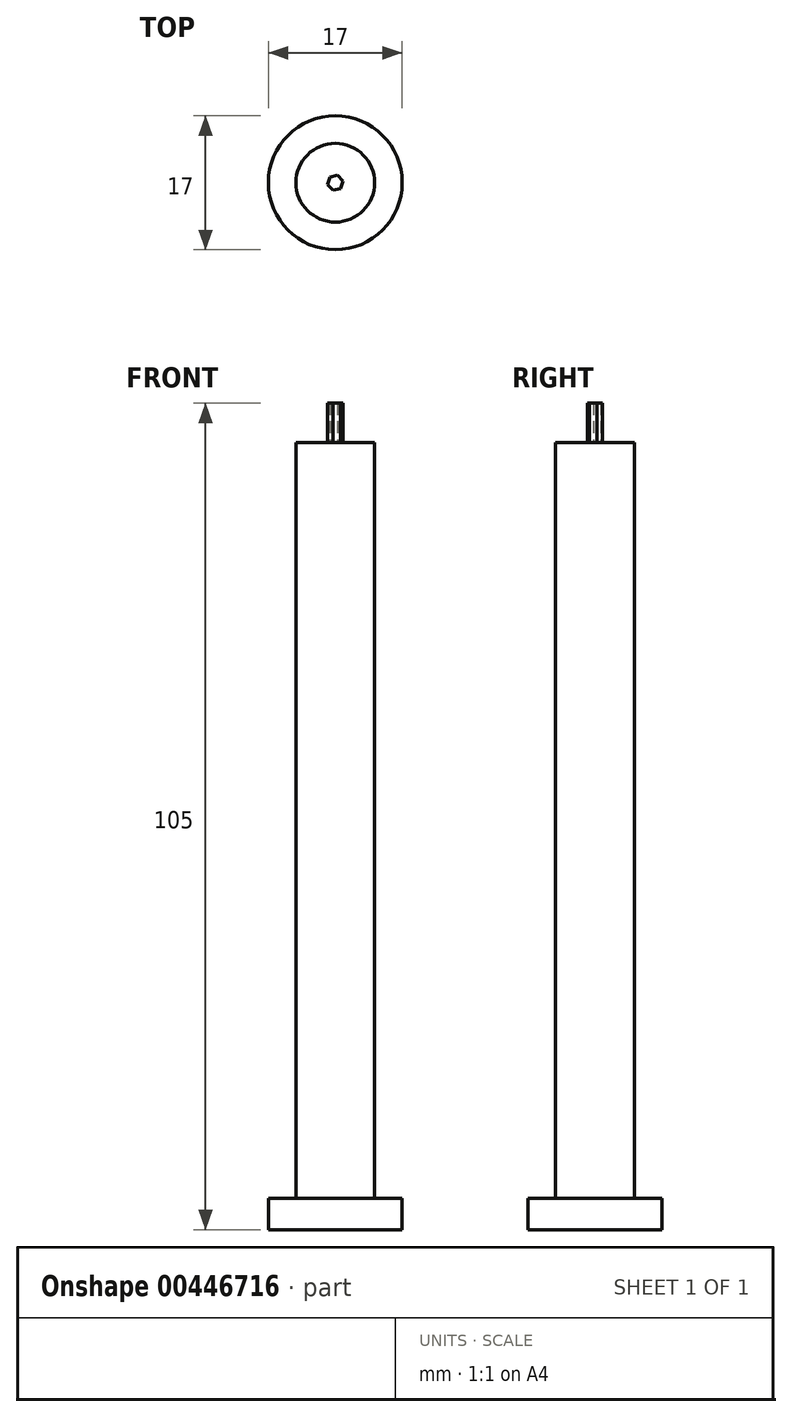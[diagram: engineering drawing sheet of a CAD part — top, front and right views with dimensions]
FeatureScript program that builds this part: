
annotation { "Feature Type Name" : "Feature", "Feature Type Description" : "" }
export const myFeature = defineFeature(function(context is Context, id is Id, definition is map)
    precondition{}
    {
        {
            var Q0;
            Q0=qCreatedBy(makeId("Top.planeOp"),FACE);
            var sketch = newSketch(context, id + "F0", { "sketchPlane" : qUnion([Q0])});
            skCircle(sketch, "E0", {"center": v(0, 0) * mm, "radius": 8.5 * mm});
            skSolve(sketch);
        }
        {
            var Q0;
            Q0=qSketchRegion(id+"F0",true);
            extrude(context, id + "F1", {"entities" : qUnion([Q0]), "depth" : 4 * mm});
        }
        {
            var Q0;
            Q0=qCreatedBy(makeId("Top.planeOp"),FACE);
            var sketch = newSketch(context, id + "F2", { "sketchPlane" : qUnion([Q0])});
            skCircle(sketch, "E1", {"center": v(0, 0) * mm, "radius": 5 * mm});
            skSolve(sketch);
        }
        {
            var Q0;
            Q0=qSketchRegion(id+"F2",true);
            extrude(context, id + "F3", {"entities" : qUnion([Q0]), "operationType" : NewBodyOperationType.ADD, "depth" : 100 * mm});
        }
        {
            var Q0;
            Q0=makeQuery(id+"F3.opExtrude","CAP_FACE",FACE,{"disambiguationData":[OSD([sQuery(id+"F2.wireOp",EDGE,"E1")])],"isStart":false});
            var sketch = newSketch(context, id + "F4", { "sketchPlane" : qUnion([Q0])});
            skCircle(sketch, "E2.cCircle", {"center": v(0, 0) * mm, "radius": 0.87 * mm, "construction": true});
            skLineSegment(sketch, "E2.0", {"start": v(0.98, 0.22) * mm, "end": v(0.67, -0.74) * mm});
            skLineSegment(sketch, "E2.1", {"start": v(0.67, -0.74) * mm, "end": v(-0.3, -0.95) * mm});
            skLineSegment(sketch, "E2.2", {"start": v(-0.3, -0.95) * mm, "end": v(-0.98, -0.22) * mm});
            skLineSegment(sketch, "E2.3", {"start": v(-0.98, -0.22) * mm, "end": v(-0.67, 0.74) * mm});
            skLineSegment(sketch, "E2.4", {"start": v(-0.67, 0.74) * mm, "end": v(0.3, 0.95) * mm});
            skLineSegment(sketch, "E2.5", {"start": v(0.3, 0.95) * mm, "end": v(0.98, 0.22) * mm});
            skPoint(sketch, "E2.0.midPoint", {"position": v(0.83, -0.26) * mm});
            skSolve(sketch);
        }
        {
            var Q0;
            Q0=makeQuery(id+"F4.imprint","IMPRINT",FACE,{"disambiguationData":[TD([[makeQuery(id+"F4.imprint","IMPRINT",EDGE,{"derivedFrom":sQuery(id+"F4.wireOp",EDGE,"E2.0")}),-1.0]])]});
            extrude(context, id + "F5", {"entities" : qUnion([Q0]), "operationType" : NewBodyOperationType.ADD, "depth" : 5 * mm});
        }
    });
